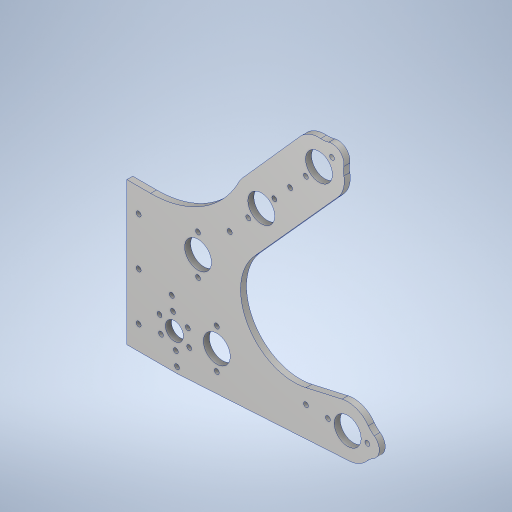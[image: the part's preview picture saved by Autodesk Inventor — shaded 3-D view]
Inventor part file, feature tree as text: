
AUTODESK INVENTOR PART (.ipt)
format: ipt  version: 2023.4 (Build 274418000, 418)  size: 381,952 bytes
history: native  units: in
note: dims shown in document units (in); Inventor stores cm internally (conversion verified against a paired STEP export)
features: sketch x2, extrude x1, hole x1, fillet x1
ambient origin geometry x8: Origin, YZ Plane, XZ Plane, XY Plane, X Axis, Y Axis, Z Axis, Center Point
bodies: Body1 (feature_tree)
feature tree (5):
  sketch  "Sketch1"  dims[d0=4.0in d2=3.0in]
  sketch  "Sketch4"  dims[d3=3.0in d4=3.0in d8=16.0in d9=12.0in d11=12.0in d13=4.5in d14=4.25in d15=0.5in d16=3.642in d17=60.0deg d63=1.125in d64=3.125in d65=1.88in d66=5.499in d67=4.018in d68=0.4688in d69=2.0in d70=0.5in d71=0.0172in d72=0.5841in d73=1.0in d74=6.0in d75=4.0in d76=1.655in d77=0.5in d79=1.0in d80=0.75in d81=1.375in d82=0.25in d83=0.0in d84=0.201in d85=0.75in d86=0.375in d87=0.25in d88=0.5635in d89=1.0in d90=0.8108in d91=1.0in d92=0.5in d93=2.3622in d95=360.0deg]
  extrude  "Extrusion2"  Depth=3.0in
  hole  "Hole2"  [1 undecoded]
  fillet  "Fillet2"  Radius=16.0in
note: 1 required parameter value undecoded (feature->parameter linkage not recoverable at this tier; creation-order binding heuristic only, values carry confidence <= 0.55)
